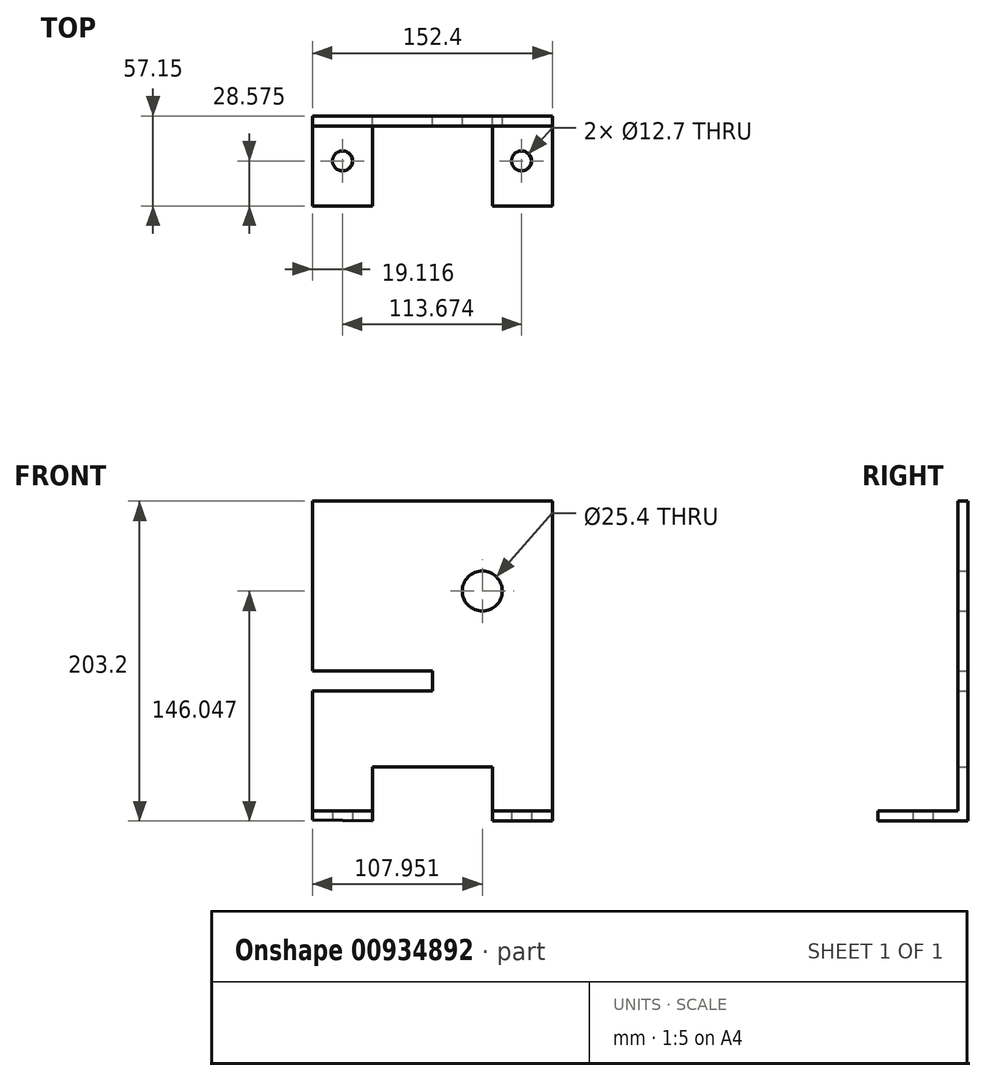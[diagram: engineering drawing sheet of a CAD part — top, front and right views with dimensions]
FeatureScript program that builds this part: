
annotation { "Feature Type Name" : "Feature", "Feature Type Description" : "" }
export const myFeature = defineFeature(function(context is Context, id is Id, definition is map)
    precondition{}
    {
        {
            var Q0;
            Q0=qCreatedBy(makeId("Front.planeOp"),FACE);
            var sketch = newSketch(context, id + "F0", { "sketchPlane" : qUnion([Q0])});
            skCircle(sketch, "E0", {"center": v(41.03, 70.84) * mm, "radius": 12.7 * mm});
            skLineSegment(sketch, "E1", {"start": v(-66.92, 127.99) * mm, "end": v(85.48, 127.99) * mm});
            skLineSegment(sketch, "E2", {"start": v(85.48, 127.99) * mm, "end": v(85.48, -75.21) * mm});
            skLineSegment(sketch, "E3", {"start": v(85.48, -75.21) * mm, "end": v(47.38, -75.21) * mm});
            skLineSegment(sketch, "E4", {"start": v(47.38, -75.21) * mm, "end": v(47.38, -40.76) * mm});
            skLineSegment(sketch, "E5", {"start": v(47.38, -40.76) * mm, "end": v(-28.82, -40.76) * mm});
            skLineSegment(sketch, "E6", {"start": v(-28.82, -40.76) * mm, "end": v(-28.82, -75.21) * mm});
            skLineSegment(sketch, "E7", {"start": v(-66.92, 127.99) * mm, "end": v(-66.92, 20.04) * mm});
            skLineSegment(sketch, "E8", {"start": v(-66.92, 20.04) * mm, "end": v(9.28, 20.04) * mm});
            skLineSegment(sketch, "E9", {"start": v(9.28, 20.04) * mm, "end": v(9.28, 7.34) * mm});
            skLineSegment(sketch, "E10", {"start": v(9.28, 7.34) * mm, "end": v(-66.92, 7.34) * mm});
            skLineSegment(sketch, "E11", {"start": v(-66.92, 7.34) * mm, "end": v(-66.92, -74.4) * mm});
            skLineSegment(sketch, "E12", {"start": v(-66.92, -74.4) * mm, "end": v(-28.82, -75.21) * mm});
            skSolve(sketch);
        }
        {
            var Q0;
            Q0 = qSketchRegion(id + "F0", true);
            extrude(context, id + "F1", {"entities" : qUnion([Q0]), "depth" : 6.35 * mm, "offsetDistance" : 25.4 * mm});
        }
        {
            var Q0;
            Q0=makeQuery(id+"F1.opExtrude","CAP_FACE",FACE,{"disambiguationData":[OSD([sQuery(id+"F0.wireOp",EDGE,"E0"),sQuery(id+"F0.wireOp",EDGE,"E1"),sQuery(id+"F0.wireOp",EDGE,"E2"),sQuery(id+"F0.wireOp",EDGE,"E3"),sQuery(id+"F0.wireOp",EDGE,"E4"),sQuery(id+"F0.wireOp",EDGE,"E5"),sQuery(id+"F0.wireOp",EDGE,"E6"),sQuery(id+"F0.wireOp",EDGE,"E7"),sQuery(id+"F0.wireOp",EDGE,"E8"),sQuery(id+"F0.wireOp",EDGE,"E9"),sQuery(id+"F0.wireOp",EDGE,"E10"),sQuery(id+"F0.wireOp",EDGE,"E11"),sQuery(id+"F0.wireOp",EDGE,"E12")])],"isStart":false});
            var sketch = newSketch(context, id + "F2", { "sketchPlane" : qUnion([Q0])});
            skLineSegment(sketch, "E13", {"start": v(-66.92, -68.86) * mm, "end": v(-28.82, -68.86) * mm});
            skLineSegment(sketch, "E14", {"start": v(47.38, -68.86) * mm, "end": v(85.48, -68.86) * mm});
            skSolve(sketch);
        }
        {
            var Q0;
            Q0 = qSketchRegion(id + "F2", true);
            var Q1;
            {var subQ0=sQuery(id+"F2.wireOp",EDGE,"E13");Q1=makeQuery(id+"F2.imprint","IMPRINT",FACE,{"disambiguationData":[TD([[makeQuery(id+"F2.imprint","IMPRINT",EDGE,{"derivedFrom":subQ0}),-1.0]])]});}
            var Q2;
            {var subQ0=sQuery(id+"F2.wireOp",EDGE,"E14");Q2=makeQuery(id+"F2.imprint","IMPRINT",FACE,{"disambiguationData":[TD([[makeQuery(id+"F2.imprint","IMPRINT",EDGE,{"derivedFrom":subQ0}),-1.0]])]});}
            extrude(context, id + "F3", {"entities" : qUnion([Q0, Q1, Q2]), "operationType" : NewBodyOperationType.ADD, "depth" : 50.8 * mm, "offsetDistance" : 25.4 * mm});
        }
        {
            var Q0;
            {var subQ0=sQuery(id+"F0.wireOp",EDGE,"E12");Q0=makeQuery(id+"F3.boolean.opBoolean","MERGE",FACE,{"derivedFrom":[makeQuery(id+"F1.opExtrude","SWEPT_FACE",FACE,{"disambiguationData":[OSD([subQ0])]}),makeQuery(id+"F3.opExtrude","SWEPT_FACE",FACE,{"disambiguationData":[OSD([subQ0])]})]});}
            var sketch = newSketch(context, id + "F4", { "sketchPlane" : qUnion([Q0])});
            skCircle(sketch, "E15", {"center": v(-46.26, 28.57) * mm, "radius": 6.35 * mm});
            skPoint(sketch, "E15.centerSnap0", {"position": v(-46.26, 57.15) * mm});
            skPoint(sketch, "E15.centerSnap1", {"position": v(-65.32, 28.57) * mm});
            skCircle(sketch, "E16", {"center": v(67.39, 28.57) * mm, "radius": 6.35 * mm});
            skPoint(sketch, "E16.centerSnap0", {"position": v(-27.2, 28.57) * mm});
            skSolve(sketch);
        }
        {
            var Q0;
            Q0=makeQuery(id+"F4.imprint","IMPRINT",FACE,{"disambiguationData":[TD([[makeQuery(id+"F4.imprint","IMPRINT",EDGE,{"derivedFrom":sQuery(id+"F4.wireOp",EDGE,"E15")}),1.0]])]});
            var Q1;
            Q1=makeQuery(id+"F4.imprint","IMPRINT",FACE,{"disambiguationData":[TD([[makeQuery(id+"F4.imprint","IMPRINT",EDGE,{"derivedFrom":sQuery(id+"F4.wireOp",EDGE,"E16")}),1.0]])]});
            extrude(context, id + "F5", {"entities" : qUnion([Q0, Q1]), "operationType" : NewBodyOperationType.REMOVE, "oppositeDirection" : true, "depth" : 25.4 * mm, "offsetDistance" : 25.4 * mm});
        }
    });
